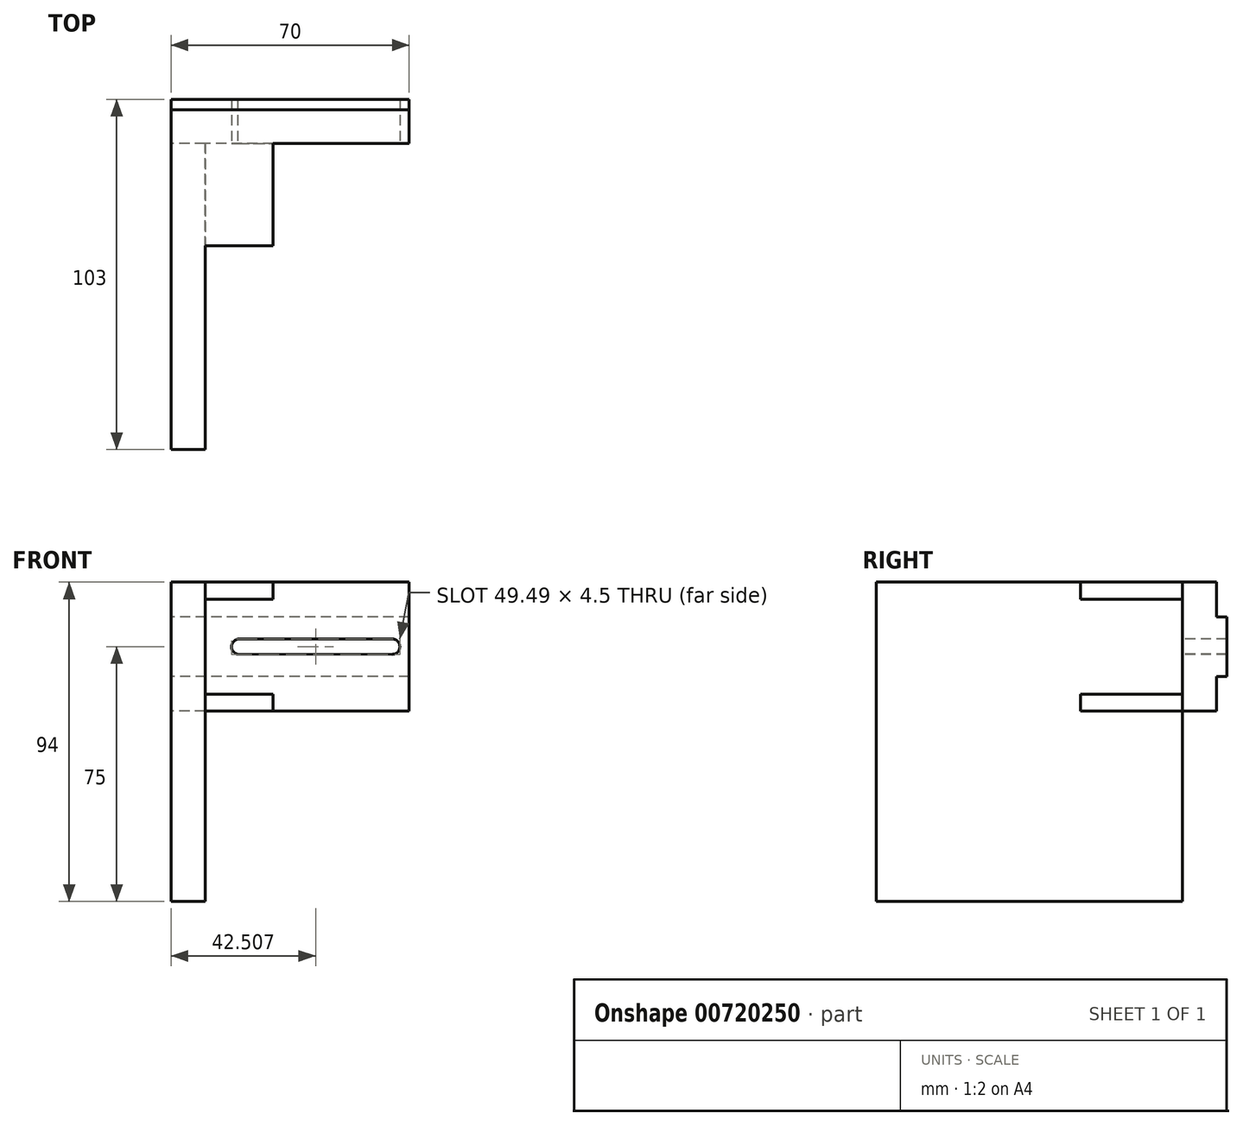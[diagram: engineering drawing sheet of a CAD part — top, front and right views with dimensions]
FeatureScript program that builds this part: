
annotation { "Feature Type Name" : "Feature", "Feature Type Description" : "" }
export const myFeature = defineFeature(function(context is Context, id is Id, definition is map)
    precondition{}
    {
        {
            var Q0;
            Q0=qCreatedBy(makeId("Front.planeOp"),FACE);
            var sketch = newSketch(context, id + "F0", { "sketchPlane" : qUnion([Q0])});
            skLineSegment(sketch, "E0.bottom", {"start": v(35, 19) * mm, "end": v(-35, 19) * mm});
            skLineSegment(sketch, "E0.top", {"start": v(35, -19) * mm, "end": v(-35, -19) * mm});
            skLineSegment(sketch, "E0.left", {"start": v(35, 19) * mm, "end": v(35, -19) * mm});
            skLineSegment(sketch, "E0.right", {"start": v(-35, 19) * mm, "end": v(-35, -19) * mm});
            skPoint(sketch, "E0.middle", {"position": v(0, 0) * mm});
            skLineSegment(sketch, "E1.bottom", {"start": v(35, 8.75) * mm, "end": v(-35, 8.75) * mm});
            skLineSegment(sketch, "E1.top", {"start": v(35, -8.75) * mm, "end": v(-35, -8.75) * mm});
            skLineSegment(sketch, "E1.left", {"start": v(35, 8.75) * mm, "end": v(35, -8.75) * mm});
            skLineSegment(sketch, "E1.right", {"start": v(-35, 8.75) * mm, "end": v(-35, -8.75) * mm});
            skSolve(sketch);
        }
        {
            var Q0;
            {var subQ0=sQuery(id+"F0.wireOp",EDGE,"E0.bottom");Q0=makeQuery(id+"F0.imprint","IMPRINT",FACE,{"disambiguationData":[TD([[makeQuery(id+"F0.imprint","IMPRINT",EDGE,{"derivedFrom":subQ0}),1.0]])]});}
            var Q1;
            Q1=makeQuery(id+"F0.imprint","IMPRINT",FACE,{"disambiguationData":[TD([[makeQuery(id+"F0.imprint","IMPRINT",EDGE,{"derivedFrom":sQuery(id+"F0.wireOp",EDGE,"E1.bottom")}),1.0]])]});
            var Q2;
            {var subQ0=sQuery(id+"F0.wireOp",EDGE,"E0.top");Q2=makeQuery(id+"F0.imprint","IMPRINT",FACE,{"disambiguationData":[TD([[makeQuery(id+"F0.imprint","IMPRINT",EDGE,{"derivedFrom":subQ0}),-1.0]])]});}
            extrude(context, id + "F1", {"entities" : qUnion([Q0, Q1, Q2]), "depth" : 10 * mm, "offsetDistance" : 25 * mm});
        }
        {
            var Q0;
            Q0=makeQuery(id+"F0.imprint","IMPRINT",FACE,{"disambiguationData":[TD([[makeQuery(id+"F0.imprint","IMPRINT",EDGE,{"derivedFrom":sQuery(id+"F0.wireOp",EDGE,"E1.bottom")}),1.0]])]});
            extrude(context, id + "F2", {"entities" : qUnion([Q0]), "operationType" : NewBodyOperationType.ADD, "oppositeDirection" : true, "depth" : 3 * mm, "offsetDistance" : 25 * mm});
        }
        {
            var Q0;
            Q0=makeQuery(id+"F1.opExtrude","CAP_FACE",FACE,{"disambiguationData":[OSD([sQuery(id+"F0.wireOp",EDGE,"E0.bottom"),sQuery(id+"F0.wireOp",EDGE,"E0.top"),sQuery(id+"F0.wireOp",EDGE,"E0.left"),sQuery(id+"F0.wireOp",EDGE,"E0.right"),sQuery(id+"F0.wireOp",EDGE,"E1.left"),sQuery(id+"F0.wireOp",EDGE,"E1.right")])],"isStart":false});
            var sketch = newSketch(context, id + "F3", { "sketchPlane" : qUnion([Q0])});
            skCircle(sketch, "E2", {"center": v(30, 0) * mm, "radius": 2.25 * mm});
            skCircle(sketch, "E3", {"center": v(-15, 0) * mm, "radius": 2.25 * mm});
            skLineSegment(sketch, "E4", {"start": v(-15, 2.25) * mm, "end": v(30, 2.25) * mm});
            skLineSegment(sketch, "E5", {"start": v(-15.5, -2.2) * mm, "end": v(30, -2.25) * mm});
            skSolve(sketch);
        }
        {
            var Q0;
            {var subQ0=sQuery(id+"F3.wireOp",EDGE,"E3");var subQ1=makeQuery(id+"F3.imprint","INTERSECT",VERTEX,{"derivedFrom":[subQ0,sQuery(id+"F3.wireOp",EDGE,"E4")]});Q0=makeQuery(id+"F3.imprint","IMPRINT",FACE,{"disambiguationData":[TD([[makeQuery(id+"F3.imprint","IMPRINT",EDGE,{"disambiguationData":[TD([[subQ1,-1.0]])],"derivedFrom":subQ0}),1.0]])]});}
            var Q1;
            {var subQ0=sQuery(id+"F3.wireOp",EDGE,"E4");Q1=makeQuery(id+"F3.imprint","IMPRINT",FACE,{"disambiguationData":[TD([[makeQuery(id+"F3.imprint","IMPRINT",EDGE,{"derivedFrom":subQ0}),-1.0]])]});}
            var Q2;
            {var subQ0=sQuery(id+"F3.wireOp",EDGE,"E2");var subQ1=makeQuery(id+"F3.imprint","INTERSECT",VERTEX,{"derivedFrom":[subQ0,sQuery(id+"F3.wireOp",EDGE,"E4")]});Q2=makeQuery(id+"F3.imprint","IMPRINT",FACE,{"disambiguationData":[TD([[makeQuery(id+"F3.imprint","IMPRINT",EDGE,{"disambiguationData":[TD([[subQ1,-1.0]])],"derivedFrom":subQ0}),1.0]])]});}
            extrude(context, id + "F4", {"entities" : qUnion([Q0, Q1, Q2]), "operationType" : NewBodyOperationType.REMOVE, "oppositeDirection" : true, "depth" : 25 * mm, "offsetDistance" : 25 * mm});
        }
        {
            var Q0;
            Q0=makeQuery(id+"F1.opExtrude","CAP_FACE",FACE,{"disambiguationData":[OSD([sQuery(id+"F0.wireOp",EDGE,"E0.bottom"),sQuery(id+"F0.wireOp",EDGE,"E0.top"),sQuery(id+"F0.wireOp",EDGE,"E0.left"),sQuery(id+"F0.wireOp",EDGE,"E0.right"),sQuery(id+"F0.wireOp",EDGE,"E1.left"),sQuery(id+"F0.wireOp",EDGE,"E1.right")])],"isStart":false});
            var sketch = newSketch(context, id + "F5", { "sketchPlane" : qUnion([Q0])});
            skLineSegment(sketch, "E6.bottom", {"start": v(-35, 19) * mm, "end": v(-25, 19) * mm});
            skLineSegment(sketch, "E6.top", {"start": v(-35, -75) * mm, "end": v(-25, -75) * mm});
            skLineSegment(sketch, "E6.left", {"start": v(-35, 19) * mm, "end": v(-35, -75) * mm});
            skLineSegment(sketch, "E6.right", {"start": v(-25, 19) * mm, "end": v(-25, -75) * mm});
            skSolve(sketch);
        }
        {
            var Q0;
            {var subQ0=sQuery(id+"F5.wireOp",EDGE,"E6.bottom");Q0=makeQuery(id+"F5.imprint","IMPRINT",FACE,{"disambiguationData":[TD([[makeQuery(id+"F5.imprint","IMPRINT",EDGE,{"derivedFrom":subQ0}),1.0]])]});}
            var Q1;
            {var subQ0=sQuery(id+"F5.wireOp",EDGE,"E6.top");Q1=makeQuery(id+"F5.imprint","IMPRINT",FACE,{"disambiguationData":[TD([[makeQuery(id+"F5.imprint","IMPRINT",EDGE,{"derivedFrom":subQ0}),1.0]])]});}
            extrude(context, id + "F6", {"entities" : qUnion([Q0, Q1]), "operationType" : NewBodyOperationType.ADD, "depth" : 90 * mm, "offsetDistance" : 25 * mm});
        }
        {
            var Q0;
            Q0=makeQuery(id+"F6.opExtrude","SWEPT_FACE",FACE,{"disambiguationData":[OSD([sQuery(id+"F5.wireOp",EDGE,"E6.right")])]});
            var sketch = newSketch(context, id + "F7", { "sketchPlane" : qUnion([Q0])});
            skLineSegment(sketch, "E7.bottom", {"start": v(-10, 19) * mm, "end": v(-100, 19) * mm});
            skLineSegment(sketch, "E7.top", {"start": v(-10, 14) * mm, "end": v(-100, 14) * mm});
            skLineSegment(sketch, "E7.left", {"start": v(-10, 19) * mm, "end": v(-10, 14) * mm});
            skLineSegment(sketch, "E7.right", {"start": v(-100, 19) * mm, "end": v(-100, 14) * mm});
            skLineSegment(sketch, "E8.bottom", {"start": v(-10, -19) * mm, "end": v(-100, -19) * mm});
            skLineSegment(sketch, "E8.top", {"start": v(-10, -14) * mm, "end": v(-100, -14) * mm});
            skLineSegment(sketch, "E8.left", {"start": v(-10, -19) * mm, "end": v(-10, -14) * mm});
            skLineSegment(sketch, "E8.right", {"start": v(-100, -19) * mm, "end": v(-100, -14) * mm});
            skLineSegment(sketch, "E9", {"start": v(-40, 19) * mm, "end": v(-40, -19) * mm});
            skSolve(sketch);
        }
        {
            var Q0;
            {var subQ0=sQuery(id+"F7.wireOp",EDGE,"E7.left");Q0=makeQuery(id+"F7.imprint","IMPRINT",FACE,{"disambiguationData":[TD([[makeQuery(id+"F7.imprint","IMPRINT",EDGE,{"derivedFrom":subQ0}),-1.0]])]});}
            var Q1;
            {var subQ0=sQuery(id+"F7.wireOp",EDGE,"E8.left");Q1=makeQuery(id+"F7.imprint","IMPRINT",FACE,{"disambiguationData":[TD([[makeQuery(id+"F7.imprint","IMPRINT",EDGE,{"derivedFrom":subQ0}),-1.0]])]});}
            extrude(context, id + "F8", {"entities" : qUnion([Q0, Q1]), "operationType" : NewBodyOperationType.ADD, "depth" : 20 * mm, "offsetDistance" : 25 * mm});
        }
    });
